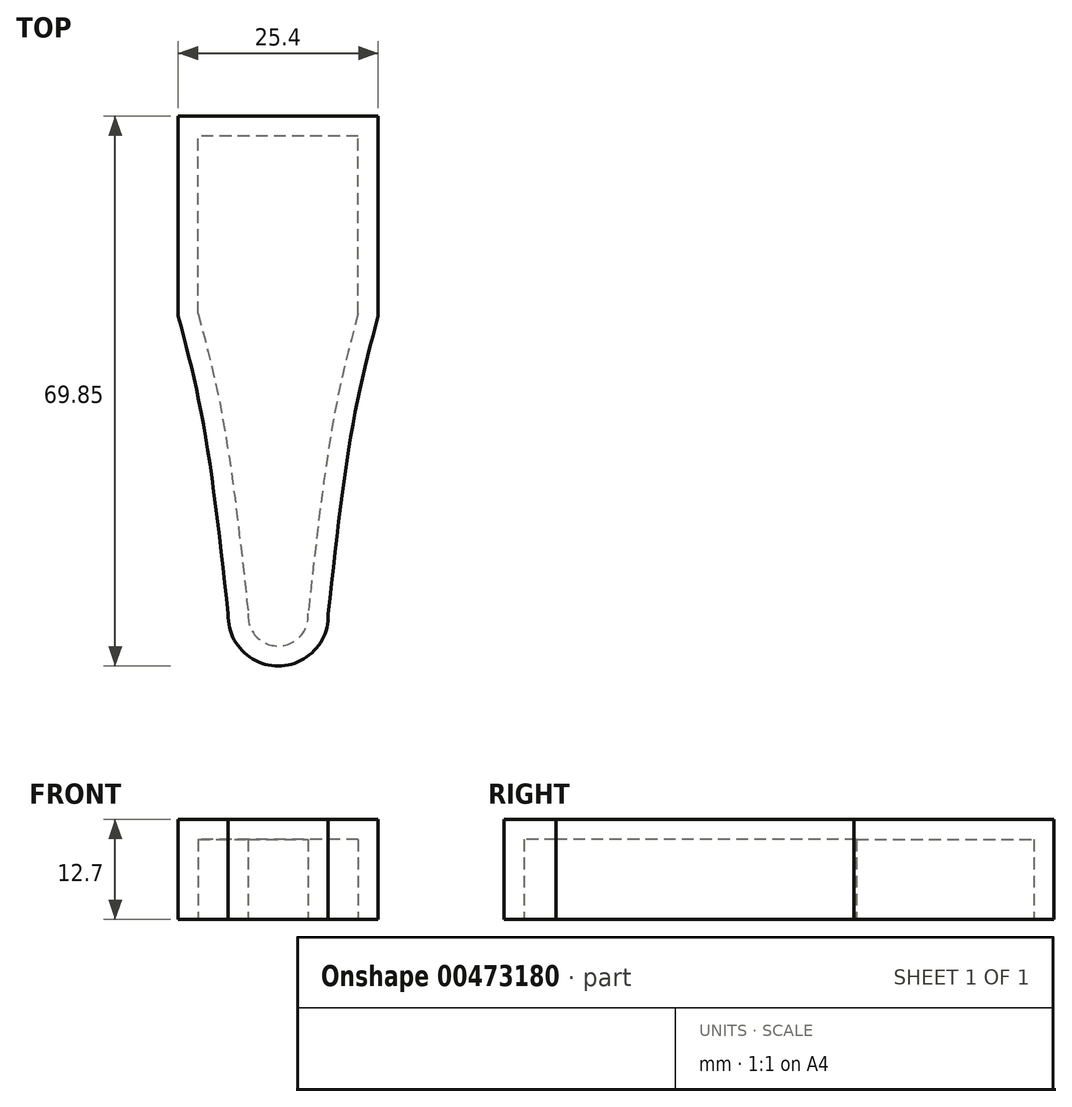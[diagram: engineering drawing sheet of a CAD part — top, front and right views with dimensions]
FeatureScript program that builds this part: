
annotation { "Feature Type Name" : "Feature", "Feature Type Description" : "" }
export const myFeature = defineFeature(function(context is Context, id is Id, definition is map)
    precondition{}
    {
        {
            var Q0;
            Q0=qCreatedBy(makeId("Top.planeOp"),FACE);
            var sketch = newSketch(context, id + "F0", { "sketchPlane" : qUnion([Q0])});
            skLineSegment(sketch, "E0.left", {"start": v(0, -50.58) * mm, "end": v(0, -50.8) * mm});
            skArc(sketch, "E1", {"start": v(0, -50.58) * mm, "mid": v(6.35, -57.15) * mm, "end": v(12.7, -50.58) * mm});
            skLineSegment(sketch, "E2.bottom", {"start": v(19.05, -12.7) * mm, "end": v(-6.35, -12.7) * mm});
            skLineSegment(sketch, "E2.top", {"start": v(19.05, 12.7) * mm, "end": v(-6.35, 12.7) * mm});
            skLineSegment(sketch, "E2.left", {"start": v(19.05, -12.7) * mm, "end": v(19.05, 12.7) * mm});
            skLineSegment(sketch, "E2.right", {"start": v(-6.35, -12.7) * mm, "end": v(-6.35, 12.7) * mm});
            skPoint(sketch, "E2.middle", {"position": v(6.35, 0) * mm});
            skPoint(sketch, "E3.orphan", {"position": v(12.7, 0) * mm});
            skPoint(sketch, "E4.orphan", {"position": v(0, 0) * mm});
            skLineSegment(sketch, "E5.bottom", {"start": v(-3.17, -12.7) * mm, "end": v(0, -12.7) * mm});
            skLineSegment(sketch, "E6.bottom", {"start": v(15.87, -12.7) * mm, "end": v(12.7, -12.7) * mm});
            skLineSegment(sketch, "E7.trimOffspring", {"start": v(12.7, -50.58) * mm, "end": v(12.7, -50.8) * mm});
            skFitSpline(sketch, "E8", {"points": [v(-6.35, -12.7) * mm, v(-3.18, -26.29) * mm, v(0, -50.58) * mm], "startDerivative": vector(7.77, -29.22) * mm, "endDerivative": vector(5.06, -45.76) * mm});
            skFitSpline(sketch, "E9", {"points": [v(19.05, -12.7) * mm, v(15.87, -26.29) * mm, v(12.7, -50.58) * mm], "startDerivative": vector(-7.77, -29.22) * mm, "endDerivative": vector(-5.06, -45.76) * mm});
            skPoint(sketch, "E5.top.start.orphan", {"position": v(-3.17, -50.58) * mm});
            skPoint(sketch, "E10.orphan", {"position": v(15.88, -50.58) * mm});
            skSolve(sketch);
        }
        {
            var Q0;
            Q0 = qSketchRegion(id + "F0", true);
            extrude(context, id + "F1", {"entities" : qUnion([Q0]), "depth" : 12.7 * mm});
        }
        {
            var Q0;
            Q0=makeQuery(id+"F1.opExtrude","CAP_FACE",FACE,{"disambiguationData":[OSD([sQuery(id+"F0.wireOp",EDGE,"E1"),sQuery(id+"F0.wireOp",EDGE,"E2.top"),sQuery(id+"F0.wireOp",EDGE,"E2.left"),sQuery(id+"F0.wireOp",EDGE,"E2.right"),sQuery(id+"F0.wireOp",EDGE,"E8"),sQuery(id+"F0.wireOp",EDGE,"E9")])],"isStart":true});
            shell(context, id + "F2", {"entities" : qUnion([Q0]), "thickness" : 2.54 * mm});
        }
    });
